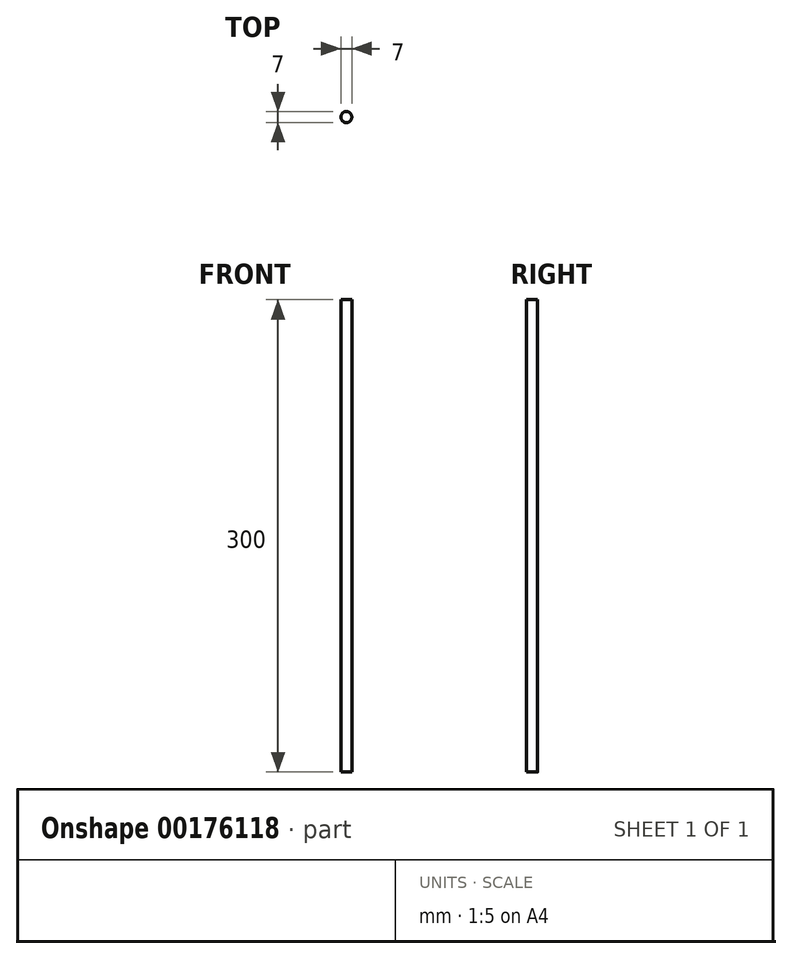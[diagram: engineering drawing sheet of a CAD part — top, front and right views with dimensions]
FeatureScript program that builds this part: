
annotation { "Feature Type Name" : "Feature", "Feature Type Description" : "" }
export const myFeature = defineFeature(function(context is Context, id is Id, definition is map)
    precondition{}
    {
        {
            var Q0;
            Q0=qCreatedBy(makeId("Top.planeOp"),FACE);
            var sketch = newSketch(context, id + "F0", { "sketchPlane" : qUnion([Q0])});
            skCircle(sketch, "E0", {"center": v(0, 0) * mm, "radius": 3.5 * mm});
            skSolve(sketch);
        }
        {
            var Q0;
            Q0=makeQuery(id+"F0.imprint","IMPRINT",FACE,{"disambiguationData":[TD([[makeQuery(id+"F0.imprint","IMPRINT",EDGE,{"derivedFrom":sQuery(id+"F0.wireOp",EDGE,"E0")}),1.0]])]});
            extrude(context, id + "F1", {"entities" : qUnion([Q0]), "depth" : 300 * mm});
        }
    });
